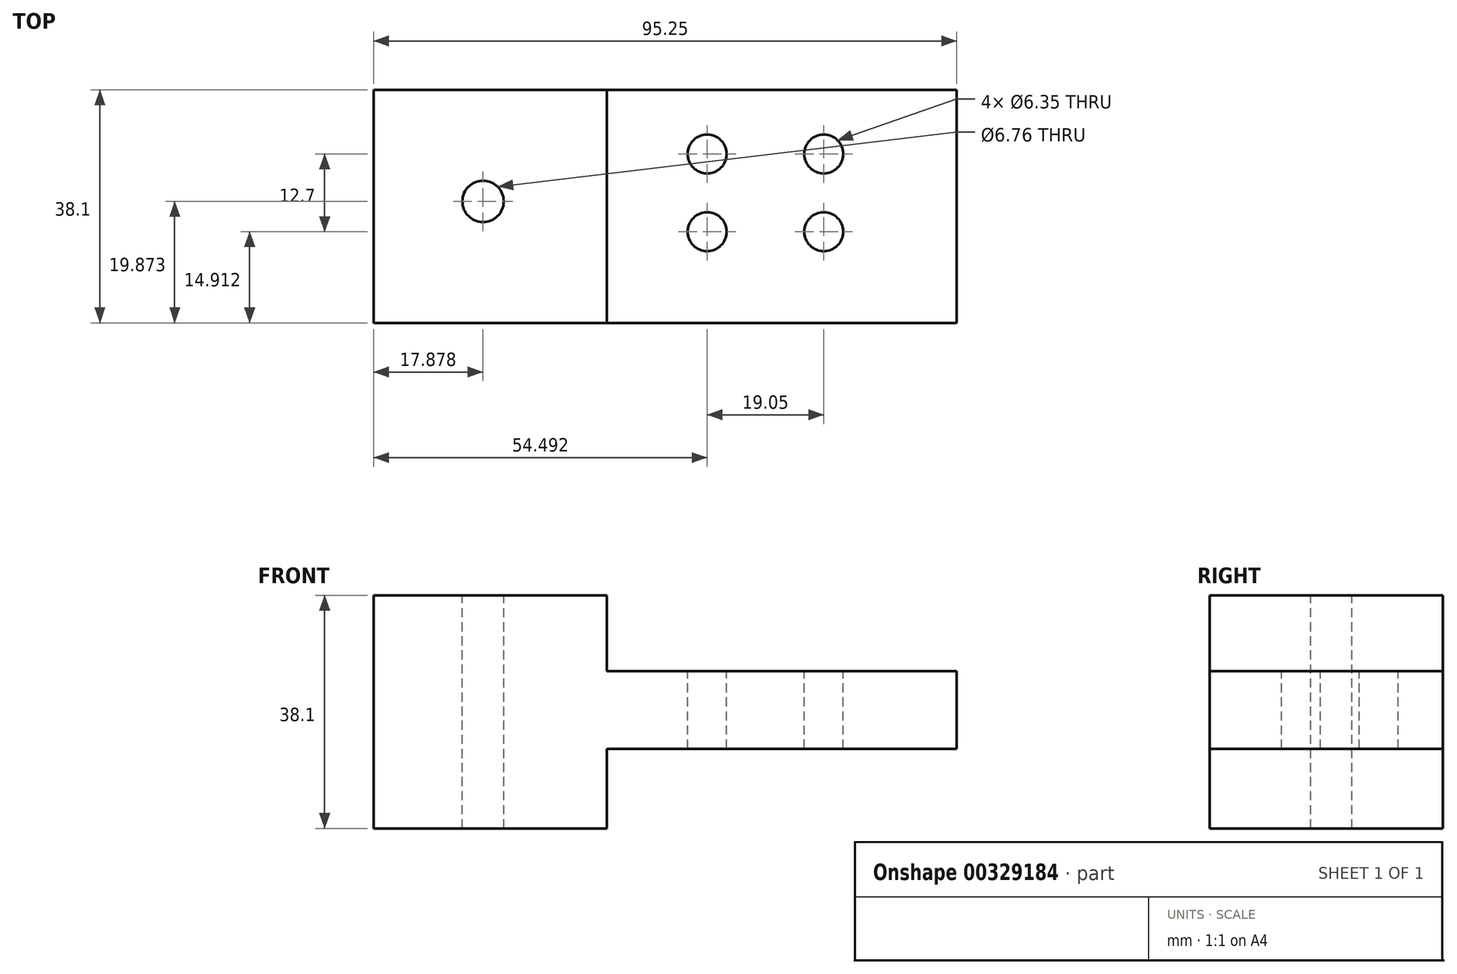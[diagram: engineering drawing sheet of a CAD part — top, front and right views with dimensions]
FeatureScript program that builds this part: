
annotation { "Feature Type Name" : "Feature", "Feature Type Description" : "" }
export const myFeature = defineFeature(function(context is Context, id is Id, definition is map)
    precondition{}
    {
        {
            var Q0;
            Q0=qCreatedBy(makeId("Front.planeOp"),FACE);
            var sketch = newSketch(context, id + "F0", { "sketchPlane" : qUnion([Q0])});
            skLineSegment(sketch, "E0", {"start": v(0, 0) * mm, "end": v(0, 38.1) * mm});
            skLineSegment(sketch, "E1", {"start": v(0, 38.1) * mm, "end": v(38.1, 38.1) * mm});
            skLineSegment(sketch, "E2", {"start": v(38.1, 38.1) * mm, "end": v(38.1, 25.72) * mm});
            skLineSegment(sketch, "E3", {"start": v(38.1, 25.72) * mm, "end": v(95.25, 25.72) * mm});
            skLineSegment(sketch, "E4", {"start": v(95.25, 25.72) * mm, "end": v(95.25, 13.02) * mm});
            skLineSegment(sketch, "E5", {"start": v(95.25, 13.02) * mm, "end": v(38.1, 13.02) * mm});
            skLineSegment(sketch, "E6", {"start": v(38.1, 13.02) * mm, "end": v(38.1, 0) * mm});
            skLineSegment(sketch, "E7", {"start": v(38.1, 0) * mm, "end": v(0, 0) * mm});
            skLineSegment(sketch, "E8", {"start": v(0, 38.1) * mm, "end": v(0, 0) * mm, "construction": true});
            skLineSegment(sketch, "E9", {"start": v(12.7, 38.1) * mm, "end": v(12.7, 0) * mm, "construction": true});
            skLineSegment(sketch, "E10", {"start": v(25.4, 38.1) * mm, "end": v(25.4, 0) * mm, "construction": true});
            skSolve(sketch);
        }
        {
            var Q0;
            Q0=makeQuery(id+"F0.imprint","IMPRINT",FACE,{"disambiguationData":[TD([[makeQuery(id+"F0.imprint","IMPRINT",EDGE,{"derivedFrom":sQuery(id+"F0.wireOp",EDGE,"E0")}),-1.0]])]});
            extrude(context, id + "F1", {"entities" : qUnion([Q0]), "depth" : 38.1 * mm});
        }
        {
            var Q0;
            Q0=makeQuery(id+"F1.opExtrude","SWEPT_FACE",FACE,{"disambiguationData":[OSD([sQuery(id+"F0.wireOp",EDGE,"E1")])]});
            var sketch = newSketch(context, id + "F2", { "sketchPlane" : qUnion([Q0])});
            skPoint(sketch, "E11", {"position": v(17.88, -18.23) * mm});
            skSolve(sketch);
        }
        {
            var Q0;
            Q0=sQuery(id+"F2.wireOp",VERTEX,"E11");
            var Q1;
            Q1=makeQuery(id+"F1.opExtrude","SWEPT_BODY",BODY,{"disambiguationData":[OSD([sQuery(id+"F0.wireOp",EDGE,"E0"),sQuery(id+"F0.wireOp",EDGE,"E1"),sQuery(id+"F0.wireOp",EDGE,"E2"),sQuery(id+"F0.wireOp",EDGE,"E3"),sQuery(id+"F0.wireOp",EDGE,"E4"),sQuery(id+"F0.wireOp",EDGE,"E5"),sQuery(id+"F0.wireOp",EDGE,"E6"),sQuery(id+"F0.wireOp",EDGE,"E7")])]});
            hole(context, id + "F3", {"style" : HoleStyle.SIMPLE, "endStyle" : HoleEndStyle.THROUGH, "standardTappedOrClearance" : lookupTablePath({ "standard" : "ANSI", "fit" : "Normal (ASME)", "size" : "1/4", "type" : "Clearance" }), "standardBlindInLast" : lookupTablePath({ "fit" : "Free", "standard" : "ANSI", "size" : "1/4", "type" : "Clearance" }), "holeDiameter" : 6.76 * mm, "tappedDepth" : 12.7 * mm, "tapClearance" : 3, "locations" : qUnion([Q0]), "scope" : qUnion([Q1])});
        }
        {
            var Q0;
            Q0=makeQuery(id+"F1.opExtrude","SWEPT_FACE",FACE,{"disambiguationData":[OSD([sQuery(id+"F0.wireOp",EDGE,"E3")])]});
            var sketch = newSketch(context, id + "F4", { "sketchPlane" : qUnion([Q0])});
            skPoint(sketch, "E12", {"position": v(54.5, -10.49) * mm});
            skPoint(sketch, "E13", {"position": v(54.5, -23.19) * mm});
            skPoint(sketch, "E14", {"position": v(73.54, -23.19) * mm});
            skPoint(sketch, "E15", {"position": v(73.54, -10.49) * mm});
            skSolve(sketch);
        }
        {
            var Q0;
            Q0=sQuery(id+"F4.wireOp",VERTEX,"E12");
            var Q1;
            Q1=sQuery(id+"F4.wireOp",VERTEX,"E13");
            var Q2;
            Q2=sQuery(id+"F4.wireOp",VERTEX,"E14");
            var Q3;
            Q3=sQuery(id+"F4.wireOp",VERTEX,"E15");
            var Q4;
            Q4=makeQuery(id+"F1.opExtrude","SWEPT_BODY",BODY,{"disambiguationData":[OSD([sQuery(id+"F0.wireOp",EDGE,"E0"),sQuery(id+"F0.wireOp",EDGE,"E1"),sQuery(id+"F0.wireOp",EDGE,"E2"),sQuery(id+"F0.wireOp",EDGE,"E3"),sQuery(id+"F0.wireOp",EDGE,"E4"),sQuery(id+"F0.wireOp",EDGE,"E5"),sQuery(id+"F0.wireOp",EDGE,"E6"),sQuery(id+"F0.wireOp",EDGE,"E7")])]});
            hole(context, id + "F5", {"style" : HoleStyle.SIMPLE, "endStyle" : HoleEndStyle.THROUGH, "holeDiameter" : 6.35 * mm, "tappedDepth" : 12.7 * mm, "tapClearance" : 3, "locations" : qUnion([Q0, Q1, Q2, Q3]), "scope" : qUnion([Q4])});
        }
        {
            var Q0;
            Q0=makeQuery(id+"F1.opExtrude","SWEPT_FACE",FACE,{"disambiguationData":[OSD([sQuery(id+"F0.wireOp",EDGE,"E3")])]});
            var sketch = newSketch(context, id + "F6", { "sketchPlane" : qUnion([Q0])});
            skSolve(sketch);
        }
        {
            var Q0;
            {var subQ0=sQuery(id+"F0.wireOp",EDGE,"E3");Q0=makeQuery(id+"F6.imprint","IMPRINT",FACE,{"disambiguationData":[TD([[makeQuery(id+"F6.imprint","IMPRINT",EDGE,{"derivedFrom":makeQuery(id+"F1.opExtrude","CAP_EDGE",EDGE,{"disambiguationData":[OSD([subQ0])],"isStart":true})}),-1.0]])]});}
            var sketch = newSketch(context, id + "F7", { "sketchPlane" : qUnion([Q0])});
            skArc(sketch, "E16", {"start": v(95.25, -38.1) * mm, "mid": v(106.64, -19.04) * mm, "end": v(95.23, 0) * mm});
            skSolve(sketch);
        }
        {
            var Q0;
            Q0=sQuery(id+"F7.wireOp",EDGE,"E16");
            extrude(context, id + "F8", {"bodyType" : ToolBodyType.SURFACE, "surfaceEntities" : qUnion([Q0]), "oppositeDirection" : true, "depth" : 12.7 * mm});
        }
    });
